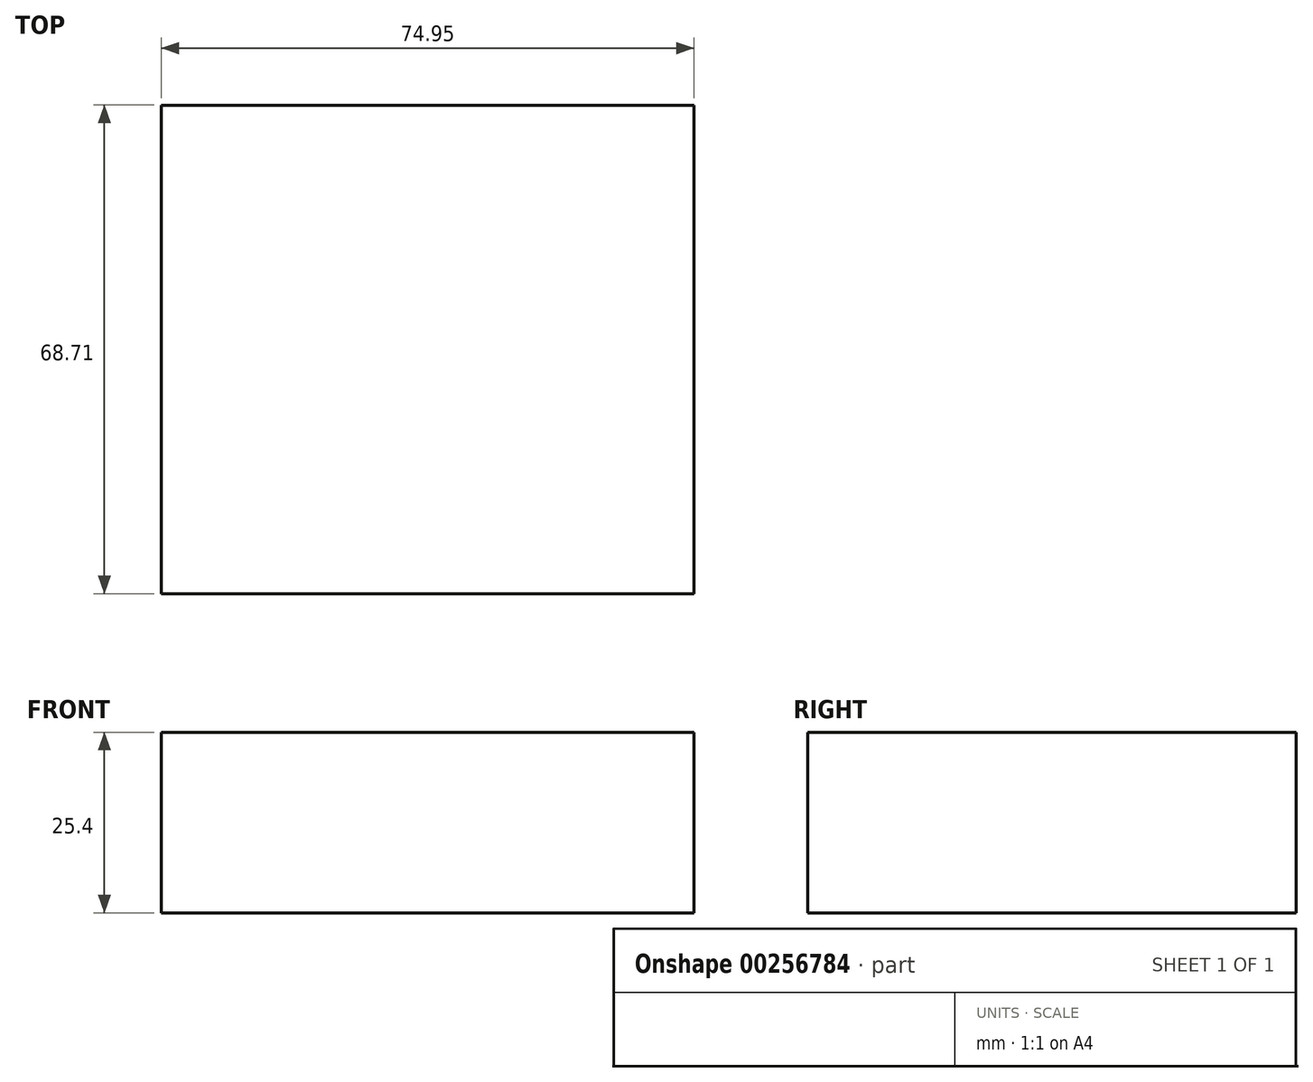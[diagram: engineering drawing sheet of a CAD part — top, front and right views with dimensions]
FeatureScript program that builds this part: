
annotation { "Feature Type Name" : "Feature", "Feature Type Description" : "" }
export const myFeature = defineFeature(function(context is Context, id is Id, definition is map)
    precondition{}
    {
        {
            var Q0;
            Q0=qCreatedBy(makeId("Top.planeOp"),FACE);
            var sketch = newSketch(context, id + "F0", { "sketchPlane" : qUnion([Q0])});
            skLineSegment(sketch, "E0.bottom", {"start": v(-33.36, 32.45) * mm, "end": v(41.6, 32.45) * mm});
            skLineSegment(sketch, "E0.top", {"start": v(-33.36, -36.26) * mm, "end": v(41.6, -36.26) * mm});
            skLineSegment(sketch, "E0.left", {"start": v(-33.36, 32.45) * mm, "end": v(-33.36, -36.26) * mm});
            skLineSegment(sketch, "E0.right", {"start": v(41.6, 32.45) * mm, "end": v(41.6, -36.26) * mm});
            skSolve(sketch);
        }
        {
            var Q0;
            Q0=makeQuery(id+"F0.imprint","IMPRINT",FACE,{"disambiguationData":[TD([[makeQuery(id+"F0.imprint","IMPRINT",EDGE,{"derivedFrom":sQuery(id+"F0.wireOp",EDGE,"E0.bottom")}),-1.0]])]});
            extrude(context, id + "F1", {"entities" : qUnion([Q0]), "depth" : 25.4 * mm});
        }
        {
            var Q0;
            Q0=qCreatedBy(makeId("Top.planeOp"),FACE);
            var sketch = newSketch(context, id + "F2", { "sketchPlane" : qUnion([Q0])});
            skArc(sketch, "E1", {"start": v(28.55, 9.22) * mm, "mid": v(1.97, 19.4) * mm, "end": v(-26.17, 15.17) * mm});
            skArc(sketch, "E2", {"start": v(-26.17, 15.17) * mm, "mid": v(0.6, 6.73) * mm, "end": v(28.55, 9.22) * mm});
            skSolve(sketch);
        }
        {
            var Q0;
            Q0 = qSketchRegion(id + "F2", true);
            extrude(context, id + "F3", {"entities" : qUnion([Q0]), "operationType" : NewBodyOperationType.REMOVE, "oppositeDirection" : true, "depth" : 25.4 * mm});
        }
        {
            var Q0;
            Q0=qCreatedBy(makeId("Top.planeOp"),FACE);
            var sketch = newSketch(context, id + "F4", { "sketchPlane" : qUnion([Q0])});
            skCircle(sketch, "E3.cCircle", {"center": v(-15.47, 12.99) * mm, "radius": 6.84 * mm, "construction": true});
            skLineSegment(sketch, "E3.0", {"start": v(-12.36, 26.3) * mm, "end": v(-5.49, 3.64) * mm});
            skLineSegment(sketch, "E3.1", {"start": v(-5.49, 3.64) * mm, "end": v(-28.55, 9.02) * mm});
            skLineSegment(sketch, "E3.2", {"start": v(-28.55, 9.02) * mm, "end": v(-12.36, 26.3) * mm});
            skPoint(sketch, "E3.0.midPoint", {"position": v(-8.92, 14.97) * mm});
            skSolve(sketch);
        }
        {
            var Q0;
            Q0 = qSketchRegion(id + "F4", true);
            extrude(context, id + "F5", {"entities" : qUnion([Q0]), "operationType" : NewBodyOperationType.ADD, "depth" : 25.4 * mm});
        }
        {
            var Q0;
            Q0=qCreatedBy(makeId("Top.planeOp"),FACE);
            var sketch = newSketch(context, id + "F6", { "sketchPlane" : qUnion([Q0])});
            skCircle(sketch, "E4", {"center": v(-17.85, 15.17) * mm, "radius": 11.15 * mm});
            skSolve(sketch);
        }
        {
            var Q0;
            Q0=makeQuery(id+"F6.imprint","IMPRINT",FACE,{"disambiguationData":[TD([[makeQuery(id+"F6.imprint","IMPRINT",EDGE,{"derivedFrom":sQuery(id+"F6.wireOp",EDGE,"E4")}),1.0]])]});
            extrude(context, id + "F7", {"entities" : qUnion([Q0]), "operationType" : NewBodyOperationType.REMOVE, "oppositeDirection" : true, "depth" : 25.4 * mm});
        }
    });
